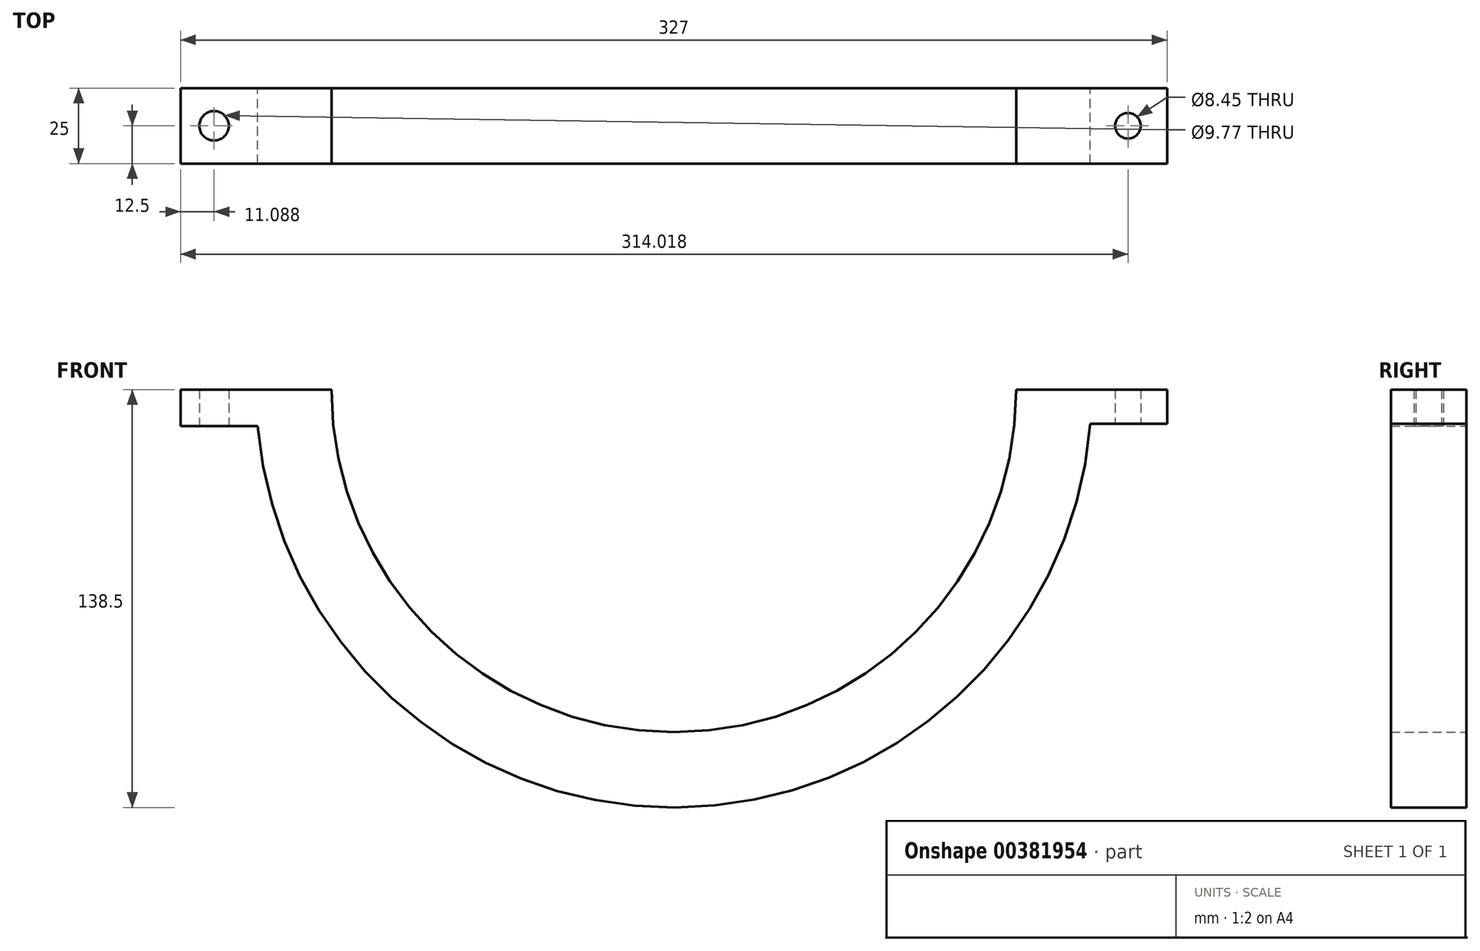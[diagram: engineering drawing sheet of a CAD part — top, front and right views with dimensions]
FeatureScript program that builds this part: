
annotation { "Feature Type Name" : "Feature", "Feature Type Description" : "" }
export const myFeature = defineFeature(function(context is Context, id is Id, definition is map)
    precondition{}
    {
        {
            var Q0;
            Q0=qCreatedBy(makeId("Front.planeOp"),FACE);
            var sketch = newSketch(context, id + "F0", { "sketchPlane" : qUnion([Q0])});
            skArc(sketch, "E0", {"start": v(-113.5, 0) * mm, "mid": v(0, -113.5) * mm, "end": v(113.5, 0) * mm});
            skLineSegment(sketch, "E1", {"start": v(-138.5, 0) * mm, "end": v(-113.5, 0) * mm});
            skArc(sketch, "E2.0", {"start": v(-137.98, -12) * mm, "mid": v(0.33, -138.5) * mm, "end": v(138.03, -11.34) * mm});
            skLineSegment(sketch, "E3.trimOffspring", {"start": v(113.5, 0) * mm, "end": v(138.5, 0) * mm});
            skPoint(sketch, "E4.middle", {"position": v(138.5, 0) * mm});
            skPoint(sketch, "E5.middle", {"position": v(-138.5, 0) * mm});
            skLineSegment(sketch, "E6", {"start": v(-138.5, 0) * mm, "end": v(-163.5, 0) * mm});
            skLineSegment(sketch, "E7.MirrorCS", {"start": v(-163.5, -12) * mm, "end": v(-137.98, -12) * mm});
            skLineSegment(sketch, "E8.MirrorCS", {"start": v(-163.5, 0) * mm, "end": v(-163.5, -12) * mm});
            skLineSegment(sketch, "E9", {"start": v(163.5, 0) * mm, "end": v(163.5, -11.34) * mm});
            skLineSegment(sketch, "E10", {"start": v(138.03, -11.34) * mm, "end": v(163.5, -11.34) * mm});
            skLineSegment(sketch, "E11", {"start": v(138.5, 0) * mm, "end": v(163.5, 0) * mm});
            skSolve(sketch);
        }
        {
            var Q0;
            Q0 = qSketchRegion(id + "F0", true);
            extrude(context, id + "F1", {"entities" : qUnion([Q0]), "endBound" : BoundingType.SYMMETRIC, "depth" : 25 * mm});
        }
        {
            var Q0;
            Q0=makeQuery(id+"F1.opExtrude","SWEPT_FACE",FACE,{"disambiguationData":[OSD([sQuery(id+"F0.wireOp",EDGE,"E10")])]});
            var sketch = newSketch(context, id + "F2", { "sketchPlane" : qUnion([Q0])});
            skCircle(sketch, "E12", {"center": v(150.52, 0) * mm, "radius": 4.23 * mm});
            skSolve(sketch);
        }
        {
            var Q0;
            Q0 = qSketchRegion(id + "F2", true);
            extrude(context, id + "F3", {"entities" : qUnion([Q0]), "operationType" : NewBodyOperationType.REMOVE, "endBound" : BoundingType.THROUGH_ALL, "oppositeDirection" : true, "depth" : 25 * mm, "offsetDistance" : 25 * mm});
        }
        {
            var Q0;
            Q0=makeQuery(id+"F1.opExtrude","SWEPT_FACE",FACE,{"disambiguationData":[OSD([sQuery(id+"F0.wireOp",EDGE,"E7.MirrorCS")])]});
            var sketch = newSketch(context, id + "F4", { "sketchPlane" : qUnion([Q0])});
            skCircle(sketch, "E13", {"center": v(-152.41, 0) * mm, "radius": 4.88 * mm});
            skSolve(sketch);
        }
        {
            var Q0;
            Q0 = qSketchRegion(id + "F4", true);
            extrude(context, id + "F5", {"entities" : qUnion([Q0]), "operationType" : NewBodyOperationType.REMOVE, "oppositeDirection" : true, "depth" : 25 * mm, "offsetDistance" : 25 * mm});
        }
    });
